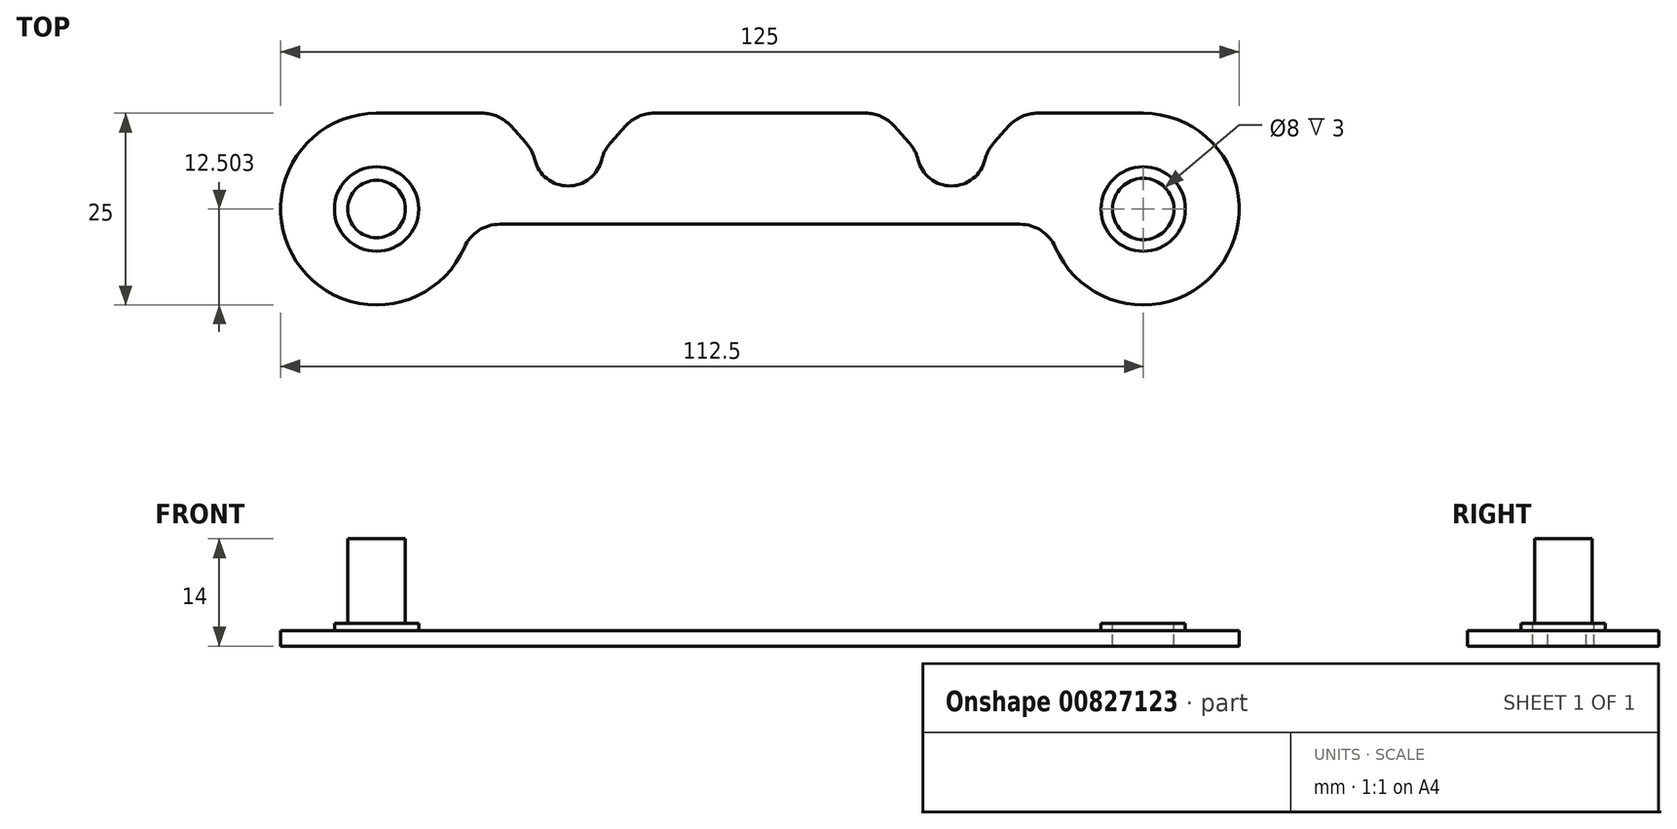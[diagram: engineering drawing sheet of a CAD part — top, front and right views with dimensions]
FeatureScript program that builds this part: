
annotation { "Feature Type Name" : "Feature", "Feature Type Description" : "" }
export const myFeature = defineFeature(function(context is Context, id is Id, definition is map)
    precondition{}
    {
        {
            var Q0;
            Q0=qCreatedBy(makeId("Front.planeOp"),FACE);
            var sketch = newSketch(context, id + "F0", { "sketchPlane" : qUnion([Q0])});
            skArc(sketch, "E0", {"start": v(29.38, 1.05) * mm, "mid": v(25, 4.5) * mm, "end": v(20.62, 1.05) * mm});
            skArc(sketch, "E1", {"start": v(-20.62, 1.05) * mm, "mid": v(-25, 4.5) * mm, "end": v(-29.38, 1.05) * mm});
            skArc(sketch, "E2", {"start": v(50, -5) * mm, "mid": v(60.46, 14.36) * mm, "end": v(38.54, 12.5) * mm});
            skArc(sketch, "E3", {"start": v(-38.54, 12.5) * mm, "mid": v(-60.46, 14.36) * mm, "end": v(-50, -5) * mm});
            skLineSegment(sketch, "E4", {"start": v(-33.96, 9.5) * mm, "end": v(33.96, 9.5) * mm});
            skCircle(sketch, "E5", {"center": v(-50, 7.5) * mm, "radius": 3.75 * mm});
            skCircle(sketch, "E6", {"center": v(50, 7.5) * mm, "radius": 4 * mm});
            skCircle(sketch, "E7", {"center": v(0, 106.6) * mm, "radius": 100 * mm, "construction": true});
            skCircle(sketch, "E8", {"center": v(-50, 7.5) * mm, "radius": 11 * mm, "construction": true});
            skCircle(sketch, "E9", {"center": v(50, 7.5) * mm, "radius": 5.5 * mm});
            skLineSegment(sketch, "E10", {"start": v(50, -5) * mm, "end": v(36.22, -5) * mm});
            skLineSegment(sketch, "E11.trimOffspring", {"start": v(13.78, -5) * mm, "end": v(-13.78, -5) * mm});
            skLineSegment(sketch, "E12.trimOffspring", {"start": v(-36.22, -5) * mm, "end": v(-50, -5) * mm});
            skLineSegment(sketch, "E13", {"start": v(20.5, 0) * mm, "end": v(0, 0) * mm, "construction": true});
            skLineSegment(sketch, "E14", {"start": v(0, 0) * mm, "end": v(-20.5, 0) * mm, "construction": true});
            skPoint(sketch, "E15.visualSharp", {"position": v(37.66, 9.5) * mm});
            skArc(sketch, "E15.filletArc", {"start": v(33.96, 9.5) * mm, "mid": v(36.7, 10.32) * mm, "end": v(38.54, 12.5) * mm});
            skPoint(sketch, "E16.visualSharp", {"position": v(-37.66, 9.5) * mm});
            skArc(sketch, "E16.filletArc", {"start": v(-38.54, 12.5) * mm, "mid": v(-36.7, 10.32) * mm, "end": v(-33.96, 9.5) * mm});
            skCircle(sketch, "E17", {"center": v(-50, 7.5) * mm, "radius": 5.5 * mm});
            skLineSegment(sketch, "E18", {"start": v(-32.51, -3.34) * mm, "end": v(-30.53, -1.14) * mm});
            skLineSegment(sketch, "E19", {"start": v(-19.47, -1.14) * mm, "end": v(-17.49, -3.34) * mm});
            skLineSegment(sketch, "E20", {"start": v(17.49, -3.34) * mm, "end": v(19.47, -1.14) * mm});
            skLineSegment(sketch, "E21", {"start": v(30.53, -1.14) * mm, "end": v(32.51, -3.34) * mm});
            skPoint(sketch, "E22.visualSharp", {"position": v(-34, -5) * mm});
            skArc(sketch, "E22.filletArc", {"start": v(-36.22, -5) * mm, "mid": v(-34.2, -4.56) * mm, "end": v(-32.51, -3.34) * mm});
            skPoint(sketch, "E23.visualSharp", {"position": v(-16, -5) * mm});
            skArc(sketch, "E23.filletArc", {"start": v(-17.49, -3.34) * mm, "mid": v(-15.8, -4.56) * mm, "end": v(-13.78, -5) * mm});
            skPoint(sketch, "E24.visualSharp", {"position": v(16, -5) * mm});
            skArc(sketch, "E24.filletArc", {"start": v(13.78, -5) * mm, "mid": v(15.8, -4.56) * mm, "end": v(17.49, -3.34) * mm});
            skPoint(sketch, "E25.visualSharp", {"position": v(34, -5) * mm});
            skArc(sketch, "E25.filletArc", {"start": v(32.51, -3.34) * mm, "mid": v(34.2, -4.56) * mm, "end": v(36.22, -5) * mm});
            skPoint(sketch, "E26.visualSharp", {"position": v(29.5, 0) * mm});
            skArc(sketch, "E26.filletArc", {"start": v(29.38, 1.05) * mm, "mid": v(29.81, -0.12) * mm, "end": v(30.53, -1.14) * mm});
            skPoint(sketch, "E27.visualSharp", {"position": v(20.5, 0) * mm});
            skArc(sketch, "E27.filletArc", {"start": v(19.47, -1.14) * mm, "mid": v(20.19, -0.12) * mm, "end": v(20.62, 1.05) * mm});
            skPoint(sketch, "E28.visualSharp", {"position": v(-20.5, 0) * mm});
            skArc(sketch, "E28.filletArc", {"start": v(-20.62, 1.05) * mm, "mid": v(-20.19, -0.12) * mm, "end": v(-19.47, -1.14) * mm});
            skPoint(sketch, "E29.visualSharp", {"position": v(-29.5, 0) * mm});
            skArc(sketch, "E29.filletArc", {"start": v(-30.53, -1.14) * mm, "mid": v(-29.81, -0.12) * mm, "end": v(-29.38, 1.05) * mm});
            skSolve(sketch);
        }
        {
            var Q0;
            {var subQ1=sQuery(id+"F0.wireOp",EDGE,"E0");Q0=makeQuery(id+"F0.imprint","IMPRINT",FACE,{"disambiguationData":[TD([[makeQuery(id+"F0.imprint","IMPRINT",EDGE,{"derivedFrom":subQ1}),-1.0]])]});}
            var Q1;
            Q1=makeQuery(id+"F0.imprint","IMPRINT",FACE,{"disambiguationData":[TD([[makeQuery(id+"F0.imprint","IMPRINT",EDGE,{"derivedFrom":sQuery(id+"F0.wireOp",EDGE,"E5")}),1.0]])]});
            var Q2;
            Q2=makeQuery(id+"F0.imprint","IMPRINT",FACE,{"disambiguationData":[TD([[makeQuery(id+"F0.imprint","IMPRINT",EDGE,{"derivedFrom":sQuery(id+"F0.wireOp",EDGE,"E5")}),-1.0]])]});
            var Q3;
            Q3=makeQuery(id+"F0.imprint","IMPRINT",FACE,{"disambiguationData":[TD([[makeQuery(id+"F0.imprint","IMPRINT",EDGE,{"derivedFrom":sQuery(id+"F0.wireOp",EDGE,"E6")}),-1.0]])]});
            extrude(context, id + "F1", {"entities" : qUnion([Q0, Q1, Q2, Q3]), "depth" : 2 * mm, "offsetDistance" : 25 * mm});
        }
        {
            var Q0;
            Q0=makeQuery(id+"F0.imprint","IMPRINT",FACE,{"disambiguationData":[TD([[makeQuery(id+"F0.imprint","IMPRINT",EDGE,{"derivedFrom":sQuery(id+"F0.wireOp",EDGE,"E5")}),1.0]])]});
            extrude(context, id + "F2", {"entities" : qUnion([Q0]), "operationType" : NewBodyOperationType.ADD, "oppositeDirection" : true, "depth" : 12 * mm, "offsetDistance" : 25 * mm});
        }
        {
            var Q0;
            Q0=makeQuery(id+"F0.imprint","IMPRINT",FACE,{"disambiguationData":[TD([[makeQuery(id+"F0.imprint","IMPRINT",EDGE,{"derivedFrom":sQuery(id+"F0.wireOp",EDGE,"E5")}),-1.0]])]});
            var Q1;
            Q1=makeQuery(id+"F0.imprint","IMPRINT",FACE,{"disambiguationData":[TD([[makeQuery(id+"F0.imprint","IMPRINT",EDGE,{"derivedFrom":sQuery(id+"F0.wireOp",EDGE,"E6")}),-1.0]])]});
            extrude(context, id + "F3", {"entities" : qUnion([Q0, Q1]), "operationType" : NewBodyOperationType.ADD, "oppositeDirection" : true, "depth" : 1 * mm, "offsetDistance" : 25 * mm});
        }
        {
            var Q0;
            Q0=makeQuery(id+"F1.opExtrude","SWEPT_BODY",BODY,{"disambiguationData":[OSD([sQuery(id+"F0.wireOp",EDGE,"8EkPLh3t-6iZm-s7Gv-l4E9-Z2ijDeSxhflq"),sQuery(id+"F0.wireOp",EDGE,"E0"),sQuery(id+"F0.wireOp",EDGE,"E1"),sQuery(id+"F0.wireOp",EDGE,"1bUsQYXy-P3kc-o97a-FX4L-6ppHi0dQ6kmW"),sQuery(id+"F0.wireOp",EDGE,"aPigvRGw-OO5B-fpMn-P9XF-XPAQLmWsaIQe"),sQuery(id+"F0.wireOp",EDGE,"OjNkqvdF-iruH-UlU3-n5YV-gxU4MGv8xxeO"),sQuery(id+"F0.wireOp",EDGE,"E2"),sQuery(id+"F0.wireOp",EDGE,"E3"),sQuery(id+"F0.wireOp",EDGE,"E4")])]});
            var Q1;
            Q1=makeQuery(id+"F1.opExtrude","CAP_EDGE",EDGE,{"disambiguationData":[OSD([sQuery(id+"F0.wireOp",EDGE,"8EkPLh3t-6iZm-s7Gv-l4E9-Z2ijDeSxhflq"),sQuery(id+"F0.wireOp",EDGE,"1bUsQYXy-P3kc-o97a-FX4L-6ppHi0dQ6kmW")])],"isStart":false});
            var Q2;
            Q2=makeQuery(id+"F1.opExtrude","CAP_EDGE",EDGE,{"disambiguationData":[OSD([sQuery(id+"F0.wireOp",EDGE,"E4")])],"isStart":true});
            transform(context, id + "F4", {"entities" : qUnion([Q0]), "transformType" : TransformType.ROTATION, "transformAxis" : qUnion([Q2]), "angle" : 90 * degree, "makeCopy" : false});
        }
    });
